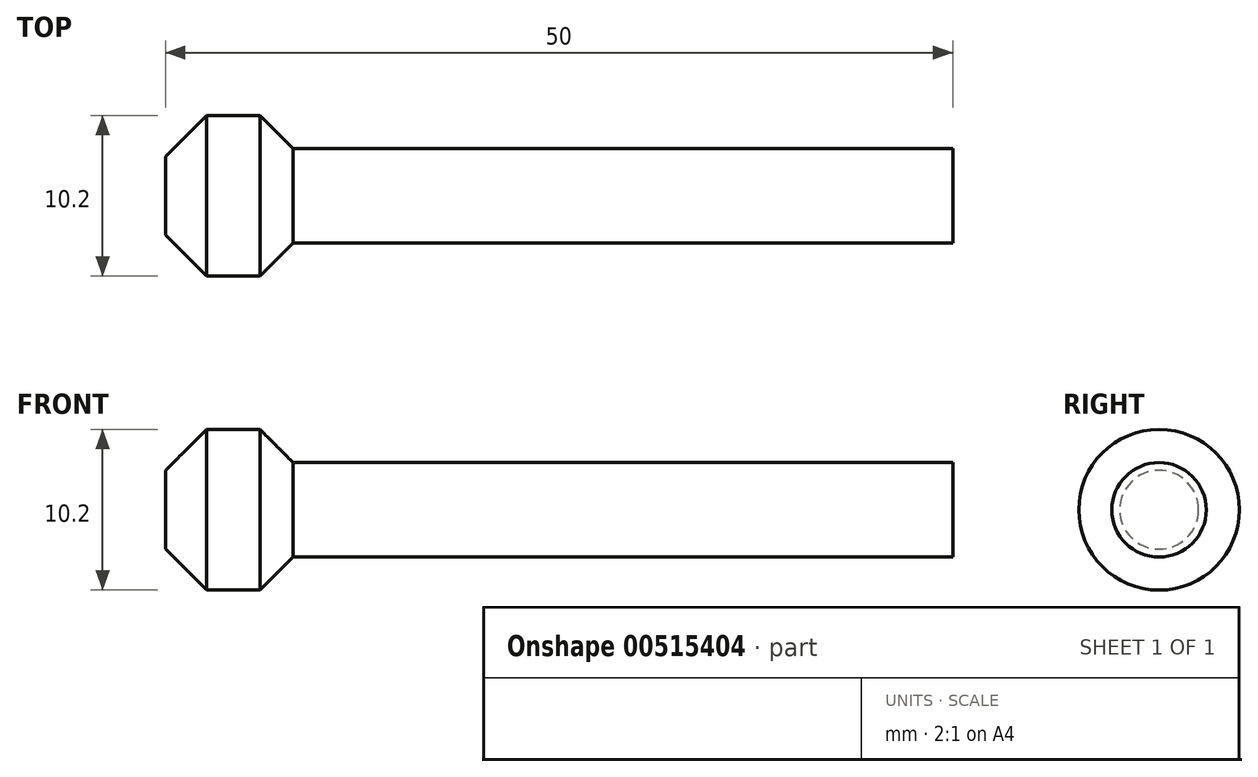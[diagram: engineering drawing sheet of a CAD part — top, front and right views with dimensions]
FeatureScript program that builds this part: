
annotation { "Feature Type Name" : "Feature", "Feature Type Description" : "" }
export const myFeature = defineFeature(function(context is Context, id is Id, definition is map)
    precondition{}
    {
        {
            var Q0;
            Q0=qCreatedBy(makeId("Front.planeOp"),FACE);
            var sketch = newSketch(context, id + "F0", { "sketchPlane" : qUnion([Q0])});
            skLineSegment(sketch, "E0", {"start": v(0, 3) * mm, "end": v(-41.9, 3) * mm});
            skLineSegment(sketch, "E1", {"start": v(0, 3) * mm, "end": v(0, 0) * mm});
            skLineSegment(sketch, "E2", {"start": v(-41.9, 3) * mm, "end": v(-44, 5.1) * mm});
            skLineSegment(sketch, "E3", {"start": v(-44, 5.1) * mm, "end": v(-47.4, 5.1) * mm});
            skLineSegment(sketch, "E4", {"start": v(-47.4, 5.1) * mm, "end": v(-50, 2.5) * mm});
            skLineSegment(sketch, "E5", {"start": v(-50, 2.5) * mm, "end": v(-50, 0) * mm});
            skLineSegment(sketch, "E6", {"start": v(-50, 0) * mm, "end": v(0, 0) * mm});
            skSolve(sketch);
        }
        {
            var Q0;
            Q0=makeQuery(id+"F0.imprint","IMPRINT",FACE,{"disambiguationData":[TD([[makeQuery(id+"F0.imprint","IMPRINT",EDGE,{"derivedFrom":sQuery(id+"F0.wireOp",EDGE,"E0")}),1.0]])]});
            var Q1;
            Q1=sQuery(id+"F0.wireOp",EDGE,"E6");
            revolve(context, id + "F1", {"entities" : qUnion([Q0]), "axis" : qUnion([Q1]), "revolveType" : RevolveType.FULL});
        }
    });
